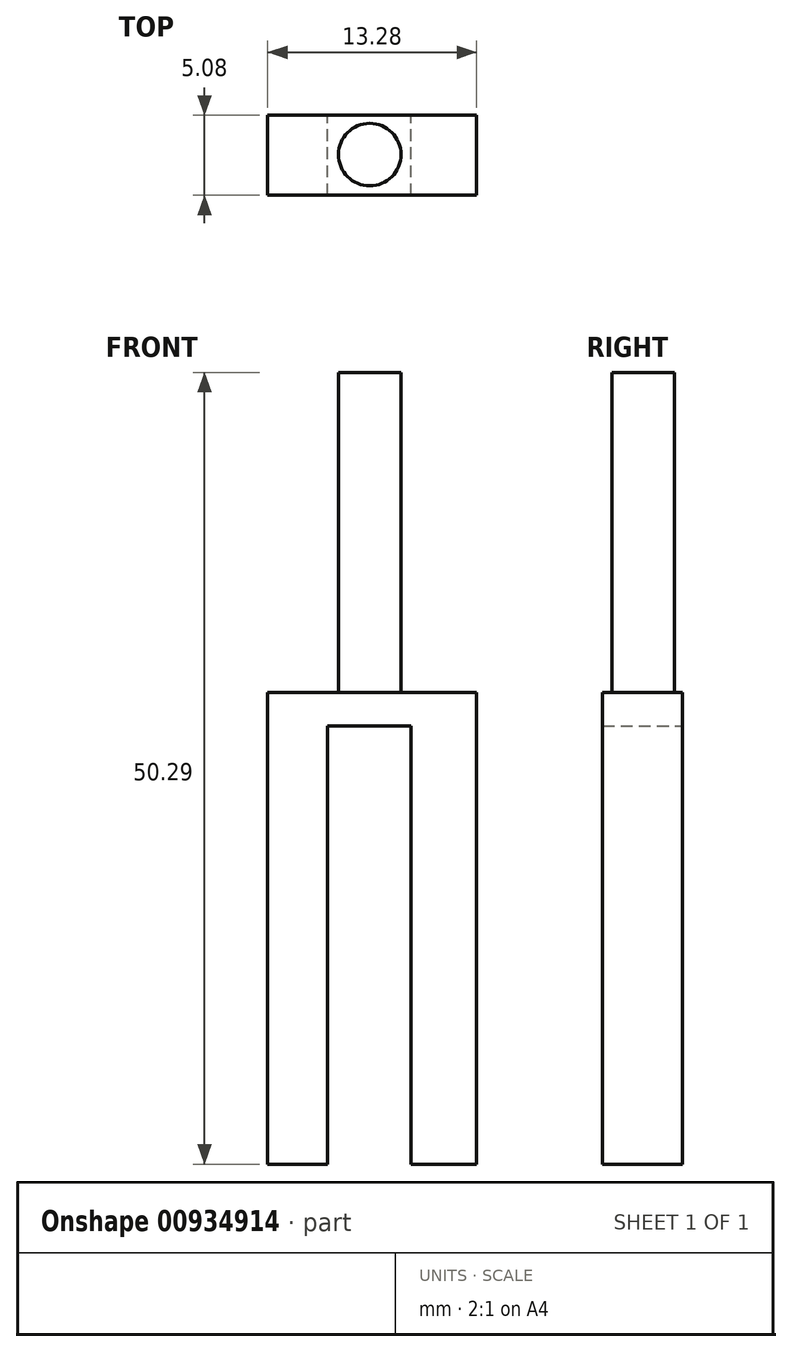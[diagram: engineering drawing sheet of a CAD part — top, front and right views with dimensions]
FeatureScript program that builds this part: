
annotation { "Feature Type Name" : "Feature", "Feature Type Description" : "" }
export const myFeature = defineFeature(function(context is Context, id is Id, definition is map)
    precondition{}
    {
        {
            var Q0;
            Q0=qCreatedBy(makeId("Front.planeOp"),FACE);
            var sketch = newSketch(context, id + "F0", { "sketchPlane" : qUnion([Q0])});
            skLineSegment(sketch, "E0.bottom", {"start": v(-18.12, 0) * mm, "end": v(-12.83, 0) * mm});
            skLineSegment(sketch, "E0.top", {"start": v(-18.12, 2.14) * mm, "end": v(-12.83, 2.14) * mm});
            skLineSegment(sketch, "E0.left", {"start": v(-18.12, 0) * mm, "end": v(-18.12, 2.14) * mm});
            skLineSegment(sketch, "E0.right", {"start": v(-12.83, 0) * mm, "end": v(-12.83, 2.14) * mm});
            skLineSegment(sketch, "E1.bottom", {"start": v(-18.12, 2.14) * mm, "end": v(-21.93, 2.14) * mm});
            skLineSegment(sketch, "E1.top", {"start": v(-18.12, -27.83) * mm, "end": v(-21.93, -27.83) * mm});
            skLineSegment(sketch, "E1.left", {"start": v(-18.12, 2.14) * mm, "end": v(-18.12, -27.83) * mm});
            skLineSegment(sketch, "E1.right", {"start": v(-21.93, 2.14) * mm, "end": v(-21.93, -27.83) * mm});
            skLineSegment(sketch, "E2.bottom", {"start": v(-12.83, 2.14) * mm, "end": v(-8.65, 2.14) * mm});
            skLineSegment(sketch, "E2.top", {"start": v(-12.83, -27.83) * mm, "end": v(-8.65, -27.83) * mm});
            skLineSegment(sketch, "E2.left", {"start": v(-12.83, 2.14) * mm, "end": v(-12.83, -27.83) * mm});
            skLineSegment(sketch, "E2.right", {"start": v(-8.65, 2.14) * mm, "end": v(-8.65, -27.83) * mm});
            skSolve(sketch);
        }
        {
            var Q0;
            {var subQ0=sQuery(id+"F0.wireOp",EDGE,"E0.bottom");Q0=makeQuery(id+"F0.imprint","IMPRINT",FACE,{"disambiguationData":[TD([[makeQuery(id+"F0.imprint","IMPRINT",EDGE,{"derivedFrom":subQ0}),1.0]])]});}
            var Q1;
            {var subQ3=sQuery(id+"F0.wireOp",EDGE,"E2.bottom");Q1=makeQuery(id+"F0.imprint","IMPRINT",FACE,{"disambiguationData":[TD([[makeQuery(id+"F0.imprint","IMPRINT",EDGE,{"derivedFrom":subQ3}),-1.0]])]});}
            var Q2;
            {var subQ3=sQuery(id+"F0.wireOp",EDGE,"E1.bottom");Q2=makeQuery(id+"F0.imprint","IMPRINT",FACE,{"disambiguationData":[TD([[makeQuery(id+"F0.imprint","IMPRINT",EDGE,{"derivedFrom":subQ3}),1.0]])]});}
            extrude(context, id + "F1", {"entities" : qUnion([Q0, Q1, Q2]), "depth" : 5.08 * mm, "offsetDistance" : 25.4 * mm});
        }
        {
            var Q0;
            Q0=makeQuery(id+"F1.opExtrude","SWEPT_FACE",FACE,{"disambiguationData":[OSD([sQuery(id+"F0.wireOp",EDGE,"E0.top"),sQuery(id+"F0.wireOp",EDGE,"E1.bottom"),sQuery(id+"F0.wireOp",EDGE,"E2.bottom")])]});
            var sketch = newSketch(context, id + "F2", { "sketchPlane" : qUnion([Q0])});
            skCircle(sketch, "E3", {"center": v(-15.44, -2.5) * mm, "radius": 1.98 * mm});
            skSolve(sketch);
        }
        {
            var Q0;
            Q0=makeQuery(id+"F2.imprint","IMPRINT",FACE,{"disambiguationData":[TD([[makeQuery(id+"F2.imprint","IMPRINT",EDGE,{"derivedFrom":sQuery(id+"F2.wireOp",EDGE,"E3")}),1.0]])]});
            extrude(context, id + "F3", {"entities" : qUnion([Q0]), "operationType" : NewBodyOperationType.ADD, "depth" : 20.32 * mm, "offsetDistance" : 25.4 * mm});
        }
    });
